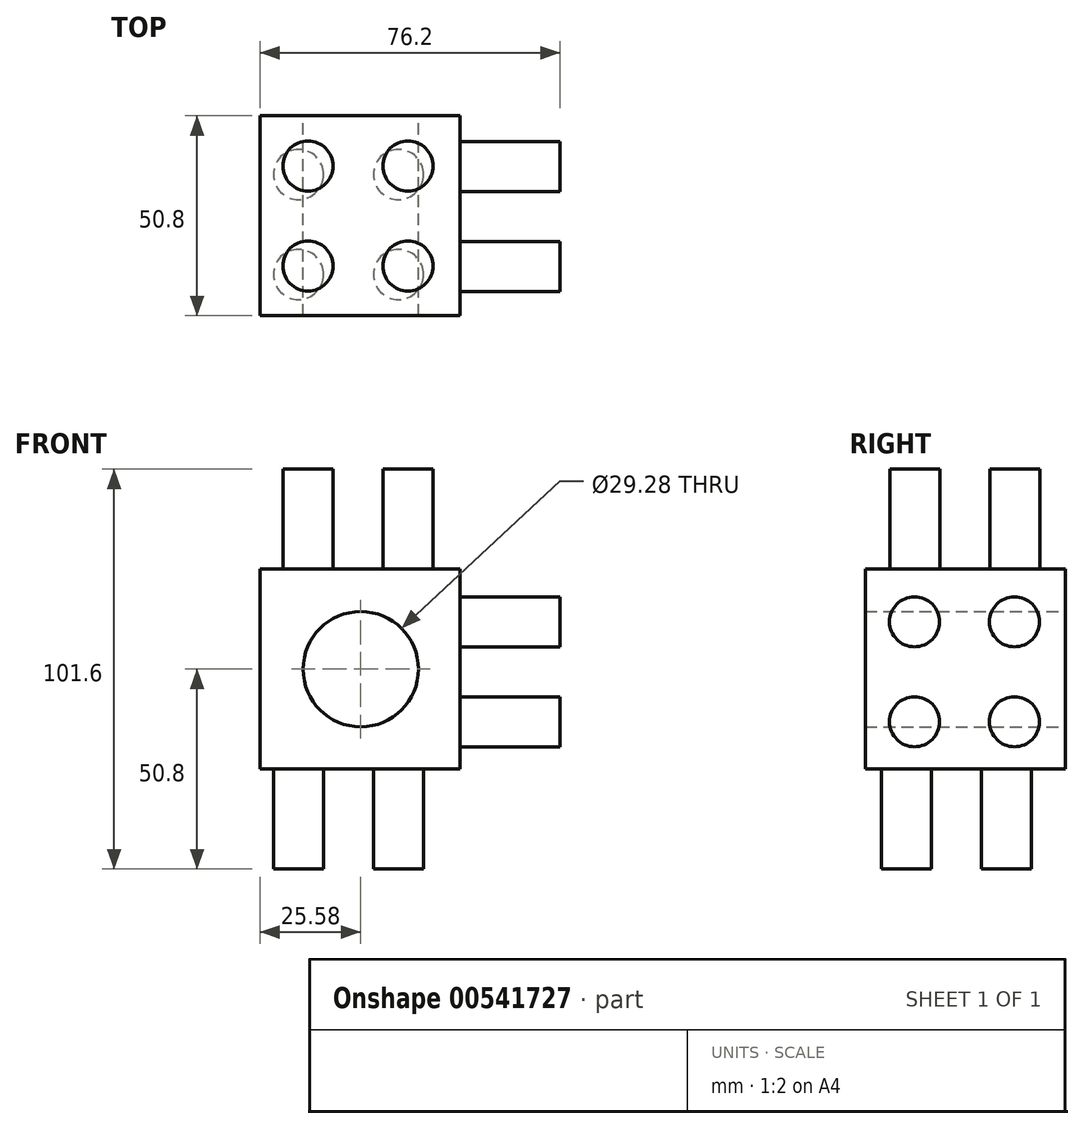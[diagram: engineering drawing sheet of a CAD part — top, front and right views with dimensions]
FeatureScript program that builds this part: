
annotation { "Feature Type Name" : "Feature", "Feature Type Description" : "" }
export const myFeature = defineFeature(function(context is Context, id is Id, definition is map)
    precondition{}
    {
        {
            var Q0;
            Q0=qCreatedBy(makeId("Front.planeOp"),FACE);
            var sketch = newSketch(context, id + "F0", { "sketchPlane" : qUnion([Q0])});
            skLineSegment(sketch, "E0.bottom", {"start": v(0, 0) * mm, "end": v(50.8, 0) * mm});
            skLineSegment(sketch, "E0.top", {"start": v(0, -50.8) * mm, "end": v(50.8, -50.8) * mm});
            skLineSegment(sketch, "E0.left", {"start": v(0, 0) * mm, "end": v(0, -50.8) * mm});
            skLineSegment(sketch, "E0.right", {"start": v(50.8, 0) * mm, "end": v(50.8, -50.8) * mm});
            skCircle(sketch, "E1", {"center": v(25.58, -25.4) * mm, "radius": 14.64 * mm});
            skPoint(sketch, "E1.centerSnap0", {"position": v(50.8, -25.4) * mm});
            skSolve(sketch);
        }
        {
            var Q0;
            Q0=makeQuery(id+"F0.imprint","IMPRINT",FACE,{"disambiguationData":[TD([[makeQuery(id+"F0.imprint","IMPRINT",EDGE,{"derivedFrom":sQuery(id+"F0.wireOp",EDGE,"E0.bottom")}),-1.0]])]});
            extrude(context, id + "F1", {"entities" : qUnion([Q0]), "depth" : 50.8 * mm, "offsetDistance" : 25.4 * mm});
        }
        {
            var Q0;
            Q0=qCreatedBy(makeId("Top.planeOp"),FACE);
            var sketch = newSketch(context, id + "F2", { "sketchPlane" : qUnion([Q0])});
            skCircle(sketch, "E2", {"center": v(12.17, -12.76) * mm, "radius": 6.35 * mm});
            skCircle(sketch, "E3.0.1.0", {"center": v(12.17, -38.16) * mm, "radius": 6.35 * mm});
            skCircle(sketch, "E3.1.0.0", {"center": v(37.57, -12.76) * mm, "radius": 6.35 * mm});
            skCircle(sketch, "E3.1.1.0", {"center": v(37.57, -38.16) * mm, "radius": 6.35 * mm});
            skLineSegment(sketch, "E3.direction1", {"start": v(12.17, -12.76) * mm, "end": v(37.57, -12.76) * mm, "construction": true});
            skLineSegment(sketch, "E3.direction2", {"start": v(12.17, -12.76) * mm, "end": v(12.17, -38.16) * mm, "construction": true});
            skSolve(sketch);
        }
        {
            var Q0;
            Q0=makeQuery(id+"F2.imprint","IMPRINT",FACE,{"disambiguationData":[TD([[makeQuery(id+"F2.imprint","IMPRINT",EDGE,{"derivedFrom":sQuery(id+"F2.wireOp",EDGE,"E3.1.0.0")}),1.0]])]});
            var Q1;
            Q1=makeQuery(id+"F2.imprint","IMPRINT",FACE,{"disambiguationData":[TD([[makeQuery(id+"F2.imprint","IMPRINT",EDGE,{"derivedFrom":sQuery(id+"F2.wireOp",EDGE,"E3.1.1.0")}),1.0]])]});
            var Q2;
            Q2=makeQuery(id+"F2.imprint","IMPRINT",FACE,{"disambiguationData":[TD([[makeQuery(id+"F2.imprint","IMPRINT",EDGE,{"derivedFrom":sQuery(id+"F2.wireOp",EDGE,"E3.0.1.0")}),1.0]])]});
            var Q3;
            Q3=makeQuery(id+"F2.imprint","IMPRINT",FACE,{"disambiguationData":[TD([[makeQuery(id+"F2.imprint","IMPRINT",EDGE,{"derivedFrom":sQuery(id+"F2.wireOp",EDGE,"E2")}),1.0]])]});
            var Q4;
            Q4=sQuery(id+"F2.wireOp",EDGE,"E2");
            var Q5;
            Q5=sQuery(id+"F2.wireOp",EDGE,"E3.0.1.0");
            var Q6;
            Q6=sQuery(id+"F2.wireOp",EDGE,"E3.1.1.0");
            var Q7;
            Q7=sQuery(id+"F2.wireOp",EDGE,"E3.1.0.0");
            extrude(context, id + "F3", {"entities" : qUnion([Q0, Q1, Q2, Q3]), "surfaceEntities" : qUnion([Q4, Q5, Q6, Q7]), "depth" : 25.4 * mm, "offsetDistance" : 25.4 * mm});
        }
        {
            var Q0;
            Q0=makeQuery(id+"F1.opExtrude","SWEPT_FACE",FACE,{"disambiguationData":[OSD([sQuery(id+"F0.wireOp",EDGE,"E0.right")])]});
            var sketch = newSketch(context, id + "F4", { "sketchPlane" : qUnion([Q0])});
            skCircle(sketch, "E4", {"center": v(-38.29, -13.36) * mm, "radius": 6.35 * mm});
            skCircle(sketch, "E5.0.1.0", {"center": v(-38.29, -38.76) * mm, "radius": 6.35 * mm});
            skCircle(sketch, "E5.1.0.0", {"center": v(-12.89, -13.36) * mm, "radius": 6.35 * mm});
            skCircle(sketch, "E5.1.1.0", {"center": v(-12.89, -38.76) * mm, "radius": 6.35 * mm});
            skLineSegment(sketch, "E5.direction1", {"start": v(-38.29, -13.36) * mm, "end": v(-12.89, -13.36) * mm, "construction": true});
            skLineSegment(sketch, "E5.direction2", {"start": v(-38.29, -13.36) * mm, "end": v(-38.29, -38.76) * mm, "construction": true});
            skSolve(sketch);
        }
        {
            var Q0;
            Q0=makeQuery(id+"F4.imprint","IMPRINT",FACE,{"disambiguationData":[TD([[makeQuery(id+"F4.imprint","IMPRINT",EDGE,{"derivedFrom":sQuery(id+"F4.wireOp",EDGE,"E5.1.1.0")}),1.0]])]});
            var Q1;
            Q1=makeQuery(id+"F4.imprint","IMPRINT",FACE,{"disambiguationData":[TD([[makeQuery(id+"F4.imprint","IMPRINT",EDGE,{"derivedFrom":sQuery(id+"F4.wireOp",EDGE,"E5.1.0.0")}),1.0]])]});
            var Q2;
            Q2=makeQuery(id+"F4.imprint","IMPRINT",FACE,{"disambiguationData":[TD([[makeQuery(id+"F4.imprint","IMPRINT",EDGE,{"derivedFrom":sQuery(id+"F4.wireOp",EDGE,"E4")}),1.0]])]});
            var Q3;
            Q3=makeQuery(id+"F4.imprint","IMPRINT",FACE,{"disambiguationData":[TD([[makeQuery(id+"F4.imprint","IMPRINT",EDGE,{"derivedFrom":sQuery(id+"F4.wireOp",EDGE,"E5.0.1.0")}),1.0]])]});
            var Q4;
            Q4=sQuery(id+"F4.wireOp",EDGE,"E4");
            var Q5;
            Q5=sQuery(id+"F4.wireOp",EDGE,"E5.1.0.0");
            var Q6;
            Q6=sQuery(id+"F4.wireOp",EDGE,"E5.1.1.0");
            var Q7;
            Q7=sQuery(id+"F4.wireOp",EDGE,"E5.0.1.0");
            extrude(context, id + "F5", {"entities" : qUnion([Q0, Q1, Q2, Q3]), "surfaceEntities" : qUnion([Q4, Q5, Q6, Q7]), "depth" : 25.4 * mm, "offsetDistance" : 25.4 * mm});
        }
        {
            var Q0;
            Q0=makeQuery(id+"F1.opExtrude","SWEPT_FACE",FACE,{"disambiguationData":[OSD([sQuery(id+"F0.wireOp",EDGE,"E0.top")])]});
            var sketch = newSketch(context, id + "F6", { "sketchPlane" : qUnion([Q0])});
            skCircle(sketch, "E6", {"center": v(9.75, 40.32) * mm, "radius": 6.35 * mm});
            skCircle(sketch, "E7.0.1.0", {"center": v(9.75, 14.92) * mm, "radius": 6.35 * mm});
            skCircle(sketch, "E7.1.0.0", {"center": v(35.15, 40.32) * mm, "radius": 6.35 * mm});
            skCircle(sketch, "E7.1.1.0", {"center": v(35.15, 14.92) * mm, "radius": 6.35 * mm});
            skLineSegment(sketch, "E7.direction1", {"start": v(9.75, 40.32) * mm, "end": v(35.15, 40.32) * mm, "construction": true});
            skLineSegment(sketch, "E7.direction2", {"start": v(9.75, 40.32) * mm, "end": v(9.75, 14.92) * mm, "construction": true});
            skSolve(sketch);
        }
        {
            var Q0;
            Q0=makeQuery(id+"F6.imprint","IMPRINT",FACE,{"disambiguationData":[TD([[makeQuery(id+"F6.imprint","IMPRINT",EDGE,{"derivedFrom":sQuery(id+"F6.wireOp",EDGE,"E6")}),1.0]])]});
            var Q1;
            Q1=makeQuery(id+"F6.imprint","IMPRINT",FACE,{"disambiguationData":[TD([[makeQuery(id+"F6.imprint","IMPRINT",EDGE,{"derivedFrom":sQuery(id+"F6.wireOp",EDGE,"E7.1.1.0")}),1.0]])]});
            var Q2;
            Q2=makeQuery(id+"F6.imprint","IMPRINT",FACE,{"disambiguationData":[TD([[makeQuery(id+"F6.imprint","IMPRINT",EDGE,{"derivedFrom":sQuery(id+"F6.wireOp",EDGE,"E7.0.1.0")}),1.0]])]});
            var Q3;
            Q3=makeQuery(id+"F6.imprint","IMPRINT",FACE,{"disambiguationData":[TD([[makeQuery(id+"F6.imprint","IMPRINT",EDGE,{"derivedFrom":sQuery(id+"F6.wireOp",EDGE,"E7.1.0.0")}),1.0]])]});
            var Q4;
            Q4=sQuery(id+"F6.wireOp",EDGE,"E7.1.1.0");
            var Q5;
            Q5=sQuery(id+"F6.wireOp",EDGE,"E7.0.1.0");
            var Q6;
            Q6=sQuery(id+"F6.wireOp",EDGE,"E6");
            var Q7;
            Q7=sQuery(id+"F6.wireOp",EDGE,"E7.1.0.0");
            extrude(context, id + "F7", {"entities" : qUnion([Q0, Q1, Q2, Q3]), "surfaceEntities" : qUnion([Q4, Q5, Q6, Q7]), "depth" : 25.4 * mm, "offsetDistance" : 25.4 * mm});
        }
        {
            var Q0;
            Q0=qCreatedBy(makeId("Right.planeOp"),FACE);
            var sketch = newSketch(context, id + "F8", { "sketchPlane" : qUnion([Q0])});
            skCircle(sketch, "E8", {"center": v(-37.5, -12.52) * mm, "radius": 6.35 * mm});
            skCircle(sketch, "E9.0.1.0", {"center": v(-37.5, -37.92) * mm, "radius": 6.35 * mm});
            skCircle(sketch, "E9.1.0.0", {"center": v(-12.1, -12.52) * mm, "radius": 6.35 * mm});
            skCircle(sketch, "E9.1.1.0", {"center": v(-12.1, -37.92) * mm, "radius": 6.35 * mm});
            skLineSegment(sketch, "E9.direction1", {"start": v(-37.5, -12.52) * mm, "end": v(-12.1, -12.52) * mm, "construction": true});
            skLineSegment(sketch, "E9.direction2", {"start": v(-37.5, -12.52) * mm, "end": v(-37.5, -37.92) * mm, "construction": true});
            skSolve(sketch);
        }
        {
            var Q0;
            Q0=makeQuery(id+"F8.imprint","IMPRINT",FACE,{"disambiguationData":[TD([[makeQuery(id+"F8.imprint","IMPRINT",EDGE,{"derivedFrom":sQuery(id+"F8.wireOp",EDGE,"E9.0.1.0")}),1.0]])]});
            var Q1;
            Q1=makeQuery(id+"F8.imprint","IMPRINT",FACE,{"disambiguationData":[TD([[makeQuery(id+"F8.imprint","IMPRINT",EDGE,{"derivedFrom":sQuery(id+"F8.wireOp",EDGE,"E9.1.0.0")}),1.0]])]});
            var Q2;
            Q2=makeQuery(id+"F8.imprint","IMPRINT",FACE,{"disambiguationData":[TD([[makeQuery(id+"F8.imprint","IMPRINT",EDGE,{"derivedFrom":sQuery(id+"F8.wireOp",EDGE,"E9.1.1.0")}),1.0]])]});
            var Q3;
            Q3=makeQuery(id+"F8.imprint","IMPRINT",FACE,{"disambiguationData":[TD([[makeQuery(id+"F8.imprint","IMPRINT",EDGE,{"derivedFrom":sQuery(id+"F8.wireOp",EDGE,"E8")}),1.0]])]});
            var Q4;
            Q4 = qConstructionFilter(qBodyType(qCreatedBy(id + "F8" ,EDGE), BodyType.WIRE), ConstructionObject.NO);
            extrude(context, id + "F9", {"entities" : qUnion([Q0, Q1, Q2, Q3]), "bodyType" : ToolBodyType.SURFACE, "surfaceEntities" : qUnion([Q4]), "oppositeDirection" : true, "depth" : 25.4 * mm, "offsetDistance" : 25.4 * mm});
        }
    });
